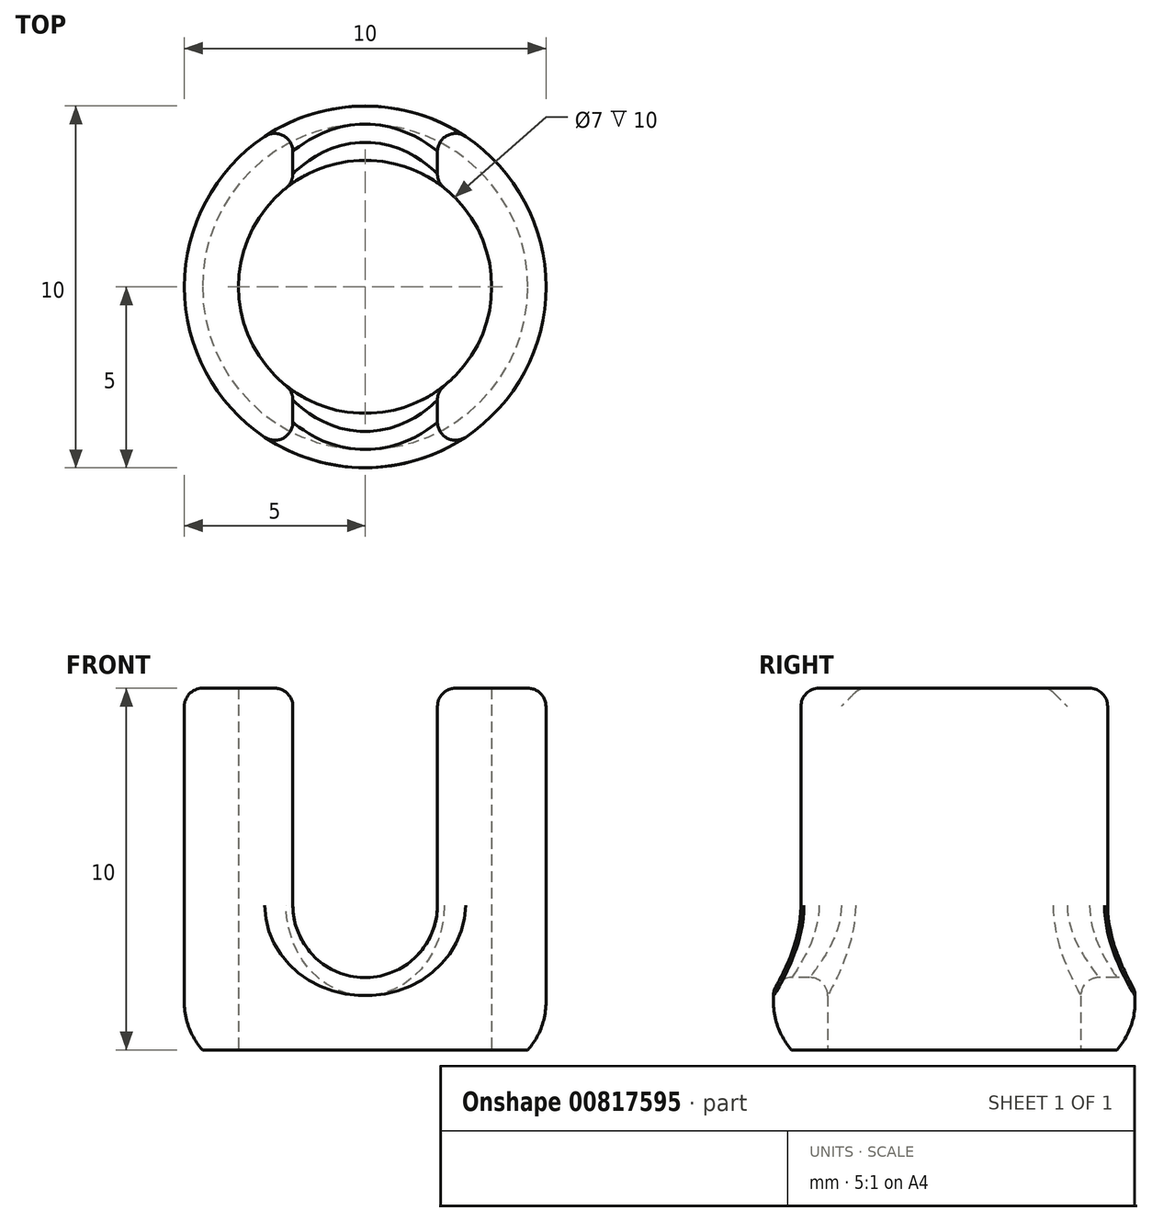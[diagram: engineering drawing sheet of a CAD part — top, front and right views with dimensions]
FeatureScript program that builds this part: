
annotation { "Feature Type Name" : "Feature", "Feature Type Description" : "" }
export const myFeature = defineFeature(function(context is Context, id is Id, definition is map)
    precondition{}
    {
        {
            var Q0;
            Q0=qCreatedBy(makeId("Top.planeOp"),FACE);
            var sketch = newSketch(context, id + "F0", { "sketchPlane" : qUnion([Q0])});
            skCircle(sketch, "E0", {"center": v(0, 0) * mm, "radius": 5 * mm});
            skCircle(sketch, "E1", {"center": v(0, 0) * mm, "radius": 3.5 * mm});
            skSolve(sketch);
        }
        {
            var Q0;
            Q0 = qSketchRegion(id + "F0", true);
            extrude(context, id + "F1", {"entities" : qUnion([Q0]), "depth" : 10 * mm, "offsetDistance" : 25 * mm});
        }
        {
            var Q0;
            Q0=qCreatedBy(makeId("Front.planeOp"),FACE);
            var sketch = newSketch(context, id + "F2", { "sketchPlane" : qUnion([Q0])});
            skLineSegment(sketch, "E2", {"start": v(0, 0) * mm, "end": v(0, 4) * mm, "construction": true});
            skCircle(sketch, "E3", {"center": v(0, 4) * mm, "radius": 2 * mm});
            skLineSegment(sketch, "E4", {"start": v(-2, 4) * mm, "end": v(0, 4) * mm, "construction": true});
            skLineSegment(sketch, "E5", {"start": v(0, 4) * mm, "end": v(2, 4) * mm, "construction": true});
            skLineSegment(sketch, "E6", {"start": v(-2, 4) * mm, "end": v(-2, 11) * mm});
            skLineSegment(sketch, "E7", {"start": v(-2, 11) * mm, "end": v(2, 11) * mm});
            skLineSegment(sketch, "E8", {"start": v(2, 11) * mm, "end": v(2, 4) * mm});
            skSolve(sketch);
        }
        {
            var Q0;
            Q0 = qSketchRegion(id + "F2", true);
            extrude(context, id + "F3", {"entities" : qUnion([Q0]), "operationType" : NewBodyOperationType.REMOVE, "endBound" : BoundingType.SYMMETRIC, "oppositeDirection" : true, "depth" : 25 * mm, "offsetDistance" : 25 * mm});
        }
        {
            var Q0;
            {var subQ0=sQuery(id+"F0.wireOp",EDGE,"E0");Q0=makeQuery(id+"F3.boolean.opBoolean","SPLIT",EDGE,{"disambiguationData":[TD([makeQuery(id+"F3.opExtrude","SWEPT_FACE",FACE,{"disambiguationData":[OSD([sQuery(id+"F2.wireOp",EDGE,"E6")])]})])],"derivedFrom":makeQuery(id+"F1.opExtrude","CAP_EDGE",EDGE,{"disambiguationData":[OSD([subQ0])],"isStart":false})});}
            var Q1;
            Q1=makeQuery(id+"F3.boolean.opBoolean","INTERSECT",EDGE,{"derivedFrom":[makeQuery(id+"F1.opExtrude","CAP_FACE",FACE,{"disambiguationData":[OSD([sQuery(id+"F0.wireOp",EDGE,"E0"),sQuery(id+"F0.wireOp",EDGE,"E1")])],"isStart":false}),makeQuery(id+"F3.opExtrude","SWEPT_FACE",FACE,{"disambiguationData":[OSD([sQuery(id+"F2.wireOp",EDGE,"E6")])]})]});
            var Q2;
            Q2=makeQuery(id+"F3.boolean.opBoolean","INTERSECT",EDGE,{"derivedFrom":[makeQuery(id+"F1.opExtrude","CAP_FACE",FACE,{"disambiguationData":[OSD([sQuery(id+"F0.wireOp",EDGE,"E0"),sQuery(id+"F0.wireOp",EDGE,"E1")])],"isStart":false}),makeQuery(id+"F3.opExtrude","SWEPT_FACE",FACE,{"disambiguationData":[OSD([sQuery(id+"F2.wireOp",EDGE,"E8")])]})]});
            var Q3;
            {var subQ0=sQuery(id+"F0.wireOp",EDGE,"E0");Q3=makeQuery(id+"F3.boolean.opBoolean","SPLIT",EDGE,{"disambiguationData":[TD([makeQuery(id+"F3.opExtrude","SWEPT_FACE",FACE,{"disambiguationData":[OSD([sQuery(id+"F2.wireOp",EDGE,"E8")])]})])],"derivedFrom":makeQuery(id+"F1.opExtrude","CAP_EDGE",EDGE,{"disambiguationData":[OSD([subQ0])],"isStart":false})});}
            var Q4;
            Q4=makeQuery(id+"F3.boolean.opBoolean","INTERSECT",EDGE,{"disambiguationData":[OD(0.0)],"derivedFrom":[makeQuery(id+"F1.opExtrude","SWEPT_FACE",FACE,{"disambiguationData":[OSD([sQuery(id+"F0.wireOp",EDGE,"E0")])]}),makeQuery(id+"F3.opExtrude","SWEPT_FACE",FACE,{"disambiguationData":[OSD([sQuery(id+"F2.wireOp",EDGE,"E6")])]})]});
            var Q5;
            Q5=makeQuery(id+"F3.boolean.opBoolean","INTERSECT",EDGE,{"disambiguationData":[OD(1.0)],"derivedFrom":[makeQuery(id+"F1.opExtrude","SWEPT_FACE",FACE,{"disambiguationData":[OSD([sQuery(id+"F0.wireOp",EDGE,"E0")])]}),makeQuery(id+"F3.opExtrude","SWEPT_FACE",FACE,{"disambiguationData":[OSD([sQuery(id+"F2.wireOp",EDGE,"E6")])]})]});
            var Q6;
            Q6=makeQuery(id+"F3.boolean.opBoolean","INTERSECT",EDGE,{"derivedFrom":[makeQuery(id+"F1.opExtrude","SWEPT_FACE",FACE,{"disambiguationData":[OSD([sQuery(id+"F0.wireOp",EDGE,"E1")])]}),makeQuery(id+"F3.opExtrude","SWEPT_FACE",FACE,{"disambiguationData":[OSD([sQuery(id+"F2.wireOp",EDGE,"E3")])]})]});
            fillet(context, id + "F4", {"entities" : qUnion([Q0, Q1, Q2, Q3, Q4, Q5, Q6]), "radius" : .5 * mm, "tangentPropagation" : true, "allowEdgeOverflow" : false});
        }
        {
            var Q0;
            Q0=makeQuery(id+"F1.opExtrude","CAP_EDGE",EDGE,{"disambiguationData":[OSD([sQuery(id+"F0.wireOp",EDGE,"E0")])],"isStart":true});
            chamfer(context, id + "F5", {"entities" : qUnion([Q0]), "width" : .5 * mm, "tangentPropagation" : true});
        }
        {
            var Q0;
            {var subQ0=sQuery(id+"F0.wireOp",EDGE,"E0");Q0=makeQuery(id+"F5.opChamfer","BLEND_EDGE",EDGE,{"blendedFrom":[makeQuery(id+"F1.opExtrude","CAP_EDGE",EDGE,{"disambiguationData":[OSD([subQ0])],"isStart":true}),makeQuery(id+"F1.opExtrude","SWEPT_FACE",FACE,{"disambiguationData":[OSD([subQ0])]})],"blendedInto":[makeQuery(id+"F1.opExtrude","SWEPT_FACE",FACE,{"disambiguationData":[OSD([subQ0])]})]});}
            fillet(context, id + "F6", {"entities" : qUnion([Q0]), "radius" : 2 * mm, "tangentPropagation" : true, "allowEdgeOverflow" : false});
        }
    });
